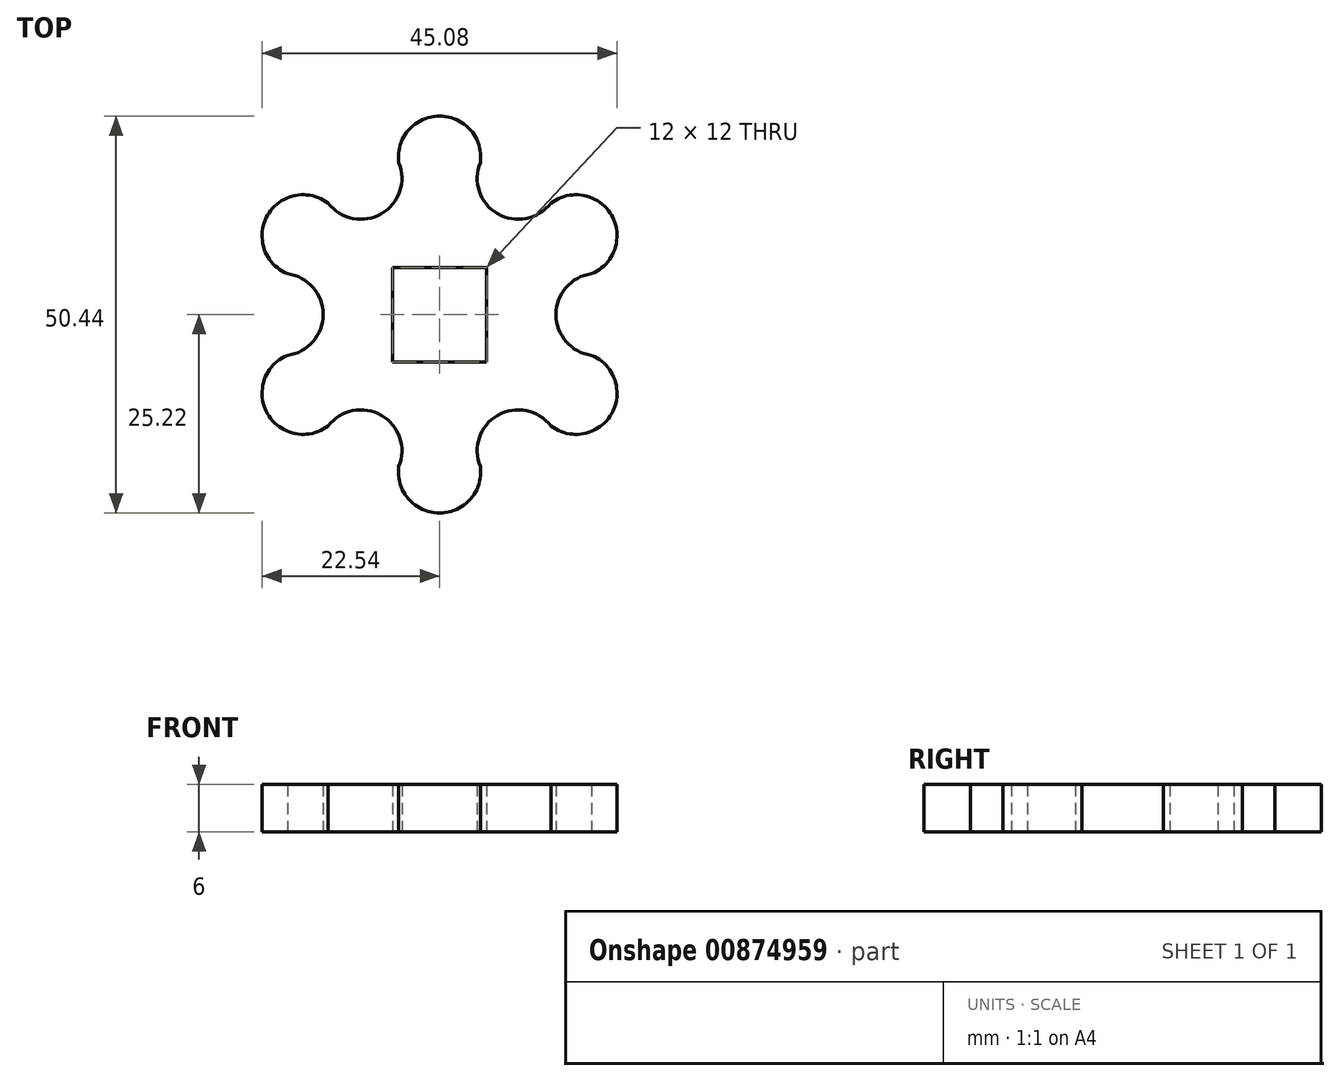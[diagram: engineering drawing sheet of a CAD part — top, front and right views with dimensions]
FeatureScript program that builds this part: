
annotation { "Feature Type Name" : "Feature", "Feature Type Description" : "" }
export const myFeature = defineFeature(function(context is Context, id is Id, definition is map)
    precondition{}
    {
        {
            var Q0;
            Q0=qCreatedBy(makeId("Top.planeOp"),FACE);
            var sketch = newSketch(context, id + "F0", { "sketchPlane" : qUnion([Q0])});
            skLineSegment(sketch, "E0.bottom", {"start": v(6, 6) * mm, "end": v(-6, 6) * mm});
            skLineSegment(sketch, "E0.top", {"start": v(6, -6) * mm, "end": v(-6, -6) * mm});
            skLineSegment(sketch, "E0.left", {"start": v(6, 6) * mm, "end": v(6, -6) * mm});
            skLineSegment(sketch, "E0.right", {"start": v(-6, 6) * mm, "end": v(-6, -6) * mm});
            skPoint(sketch, "E0.middle", {"position": v(0, 0) * mm});
            skCircle(sketch, "E1", {"center": v(0, 0) * mm, "radius": 20 * mm});
            skCircle(sketch, "E2", {"center": v(0, 20) * mm, "radius": 5.22 * mm});
            skCircle(sketch, "E3.1.0", {"center": v(-10, 17.32) * mm, "radius": 5.22 * mm});
            skCircle(sketch, "E3.2.0", {"center": v(-17.32, 10) * mm, "radius": 5.22 * mm});
            skCircle(sketch, "E3.3.0", {"center": v(-20, 0) * mm, "radius": 5.22 * mm});
            skCircle(sketch, "E3.4.0", {"center": v(-17.32, -10) * mm, "radius": 5.22 * mm});
            skCircle(sketch, "E3.5.0", {"center": v(-10, -17.32) * mm, "radius": 5.22 * mm});
            skCircle(sketch, "E3.6.0", {"center": v(0, -20) * mm, "radius": 5.22 * mm});
            skCircle(sketch, "E3.7.0", {"center": v(10, -17.32) * mm, "radius": 5.22 * mm});
            skCircle(sketch, "E3.8.0", {"center": v(17.32, -10) * mm, "radius": 5.22 * mm});
            skCircle(sketch, "E3.9.0", {"center": v(20, 0) * mm, "radius": 5.22 * mm});
            skCircle(sketch, "E3.10.0", {"center": v(17.32, 10) * mm, "radius": 5.22 * mm});
            skCircle(sketch, "E3.11.0", {"center": v(10, 17.32) * mm, "radius": 5.22 * mm});
            skPoint(sketch, "E4", {"position": v(5.18, 19.32) * mm});
            skSolve(sketch);
        }
        {
            var Q0;
            Q0=makeQuery(id+"F0.imprint","IMPRINT",FACE,{"disambiguationData":[TD([[makeQuery(id+"F0.imprint","IMPRINT",EDGE,{"derivedFrom":sQuery(id+"F0.wireOp",EDGE,"E0.bottom")}),-1.0]])]});
            var Q1;
            {var subQ0=sQuery(id+"F0.wireOp",EDGE,"E3.10.0");var subQ1=sQuery(id+"F0.wireOp",EDGE,"E3.9.0");var subQ6=makeQuery(id+"F0.imprint","INTERSECT",VERTEX,{"derivedFrom":[subQ1,subQ0]});Q1=makeQuery(id+"F0.imprint","IMPRINT",FACE,{"disambiguationData":[TD([[makeQuery(id+"F0.imprint","IMPRINT",EDGE,{"disambiguationData":[TD([[subQ6,1.0]])],"derivedFrom":subQ0}),1.0]])]});}
            var Q2;
            {var subQ1=sQuery(id+"F0.wireOp",EDGE,"E2");var subQ4=sQuery(id+"F0.wireOp",EDGE,"E3.1.0");var subQ6=makeQuery(id+"F0.imprint","INTERSECT",VERTEX,{"derivedFrom":[subQ1,subQ4]});Q2=makeQuery(id+"F0.imprint","IMPRINT",FACE,{"disambiguationData":[TD([[makeQuery(id+"F0.imprint","IMPRINT",EDGE,{"disambiguationData":[TD([[subQ6,-1.0]])],"derivedFrom":subQ1}),1.0]])]});}
            var Q3;
            {var subQ1=sQuery(id+"F0.wireOp",EDGE,"E3.8.0");var subQ4=sQuery(id+"F0.wireOp",EDGE,"E3.7.0");var subQ6=makeQuery(id+"F0.imprint","INTERSECT",VERTEX,{"derivedFrom":[subQ4,subQ1]});Q3=makeQuery(id+"F0.imprint","IMPRINT",FACE,{"disambiguationData":[TD([[makeQuery(id+"F0.imprint","IMPRINT",EDGE,{"disambiguationData":[TD([[subQ6,1.0]])],"derivedFrom":subQ1}),1.0]])]});}
            var Q4;
            {var subQ0=sQuery(id+"F0.wireOp",EDGE,"E3.4.0");var subQ1=sQuery(id+"F0.wireOp",EDGE,"E3.3.0");var subQ6=makeQuery(id+"F0.imprint","INTERSECT",VERTEX,{"derivedFrom":[subQ1,subQ0]});Q4=makeQuery(id+"F0.imprint","IMPRINT",FACE,{"disambiguationData":[TD([[makeQuery(id+"F0.imprint","IMPRINT",EDGE,{"disambiguationData":[TD([[subQ6,1.0]])],"derivedFrom":subQ0}),1.0]])]});}
            var Q5;
            {var subQ0=sQuery(id+"F0.wireOp",EDGE,"E3.2.0");var subQ1=sQuery(id+"F0.wireOp",EDGE,"E3.1.0");var subQ6=makeQuery(id+"F0.imprint","INTERSECT",VERTEX,{"derivedFrom":[subQ1,subQ0]});Q5=makeQuery(id+"F0.imprint","IMPRINT",FACE,{"disambiguationData":[TD([[makeQuery(id+"F0.imprint","IMPRINT",EDGE,{"disambiguationData":[TD([[subQ6,1.0]])],"derivedFrom":subQ0}),1.0]])]});}
            var Q6;
            {var subQ0=sQuery(id+"F0.wireOp",EDGE,"E2");var subQ1=sQuery(id+"F0.wireOp",EDGE,"E1");var subQ2=makeQuery(id+"F0.imprint","INTERSECT",VERTEX,{"derivedFrom":[subQ1,subQ0,sQuery(id+"F0.wireOp",EDGE,"E3.11.0")]});Q6=makeQuery(id+"F0.imprint","IMPRINT",FACE,{"disambiguationData":[TD([[makeQuery(id+"F0.imprint","IMPRINT",EDGE,{"disambiguationData":[TD([[subQ2,-1.0]])],"derivedFrom":subQ1}),-1.0]])]});}
            var Q7;
            {var subQ0=sQuery(id+"F0.wireOp",EDGE,"E3.10.0");var subQ1=sQuery(id+"F0.wireOp",EDGE,"E1");var subQ2=makeQuery(id+"F0.imprint","INTERSECT",VERTEX,{"derivedFrom":[subQ1,sQuery(id+"F0.wireOp",EDGE,"E3.9.0"),subQ0]});Q7=makeQuery(id+"F0.imprint","IMPRINT",FACE,{"disambiguationData":[TD([[makeQuery(id+"F0.imprint","IMPRINT",EDGE,{"disambiguationData":[TD([[subQ2,-1.0]])],"derivedFrom":subQ1}),-1.0]])]});}
            var Q8;
            {var subQ0=sQuery(id+"F0.wireOp",EDGE,"E3.8.0");var subQ1=sQuery(id+"F0.wireOp",EDGE,"E1");var subQ2=makeQuery(id+"F0.imprint","INTERSECT",VERTEX,{"derivedFrom":[subQ1,subQ0,sQuery(id+"F0.wireOp",EDGE,"E3.9.0")]});Q8=makeQuery(id+"F0.imprint","IMPRINT",FACE,{"disambiguationData":[TD([[makeQuery(id+"F0.imprint","IMPRINT",EDGE,{"disambiguationData":[TD([[subQ2,1.0]])],"derivedFrom":subQ1}),-1.0]])]});}
            var Q9;
            {var subQ0=sQuery(id+"F0.wireOp",EDGE,"E3.6.0");var subQ1=sQuery(id+"F0.wireOp",EDGE,"E3.5.0");var subQ6=makeQuery(id+"F0.imprint","INTERSECT",VERTEX,{"derivedFrom":[subQ1,subQ0]});Q9=makeQuery(id+"F0.imprint","IMPRINT",FACE,{"disambiguationData":[TD([[makeQuery(id+"F0.imprint","IMPRINT",EDGE,{"disambiguationData":[TD([[subQ6,1.0]])],"derivedFrom":subQ0}),1.0]])]});}
            var Q10;
            {var subQ0=sQuery(id+"F0.wireOp",EDGE,"E3.6.0");var subQ1=sQuery(id+"F0.wireOp",EDGE,"E1");var subQ2=makeQuery(id+"F0.imprint","INTERSECT",VERTEX,{"derivedFrom":[subQ1,sQuery(id+"F0.wireOp",EDGE,"E3.5.0"),subQ0]});Q10=makeQuery(id+"F0.imprint","IMPRINT",FACE,{"disambiguationData":[TD([[makeQuery(id+"F0.imprint","IMPRINT",EDGE,{"disambiguationData":[TD([[subQ2,-1.0]])],"derivedFrom":subQ1}),-1.0]])]});}
            var Q11;
            {var subQ0=sQuery(id+"F0.wireOp",EDGE,"E3.4.0");var subQ1=sQuery(id+"F0.wireOp",EDGE,"E1");var subQ2=makeQuery(id+"F0.imprint","INTERSECT",VERTEX,{"derivedFrom":[subQ1,sQuery(id+"F0.wireOp",EDGE,"E3.3.0"),subQ0]});Q11=makeQuery(id+"F0.imprint","IMPRINT",FACE,{"disambiguationData":[TD([[makeQuery(id+"F0.imprint","IMPRINT",EDGE,{"disambiguationData":[TD([[subQ2,-1.0]])],"derivedFrom":subQ1}),-1.0]])]});}
            var Q12;
            {var subQ0=sQuery(id+"F0.wireOp",EDGE,"E3.2.0");var subQ1=sQuery(id+"F0.wireOp",EDGE,"E1");var subQ2=makeQuery(id+"F0.imprint","INTERSECT",VERTEX,{"derivedFrom":[subQ1,sQuery(id+"F0.wireOp",EDGE,"E3.1.0"),subQ0]});Q12=makeQuery(id+"F0.imprint","IMPRINT",FACE,{"disambiguationData":[TD([[makeQuery(id+"F0.imprint","IMPRINT",EDGE,{"disambiguationData":[TD([[subQ2,-1.0]])],"derivedFrom":subQ1}),-1.0]])]});}
            extrude(context, id + "F1", {"entities" : qUnion([Q0, Q1, Q2, Q3, Q4, Q5, Q6, Q7, Q8, Q9, Q10, Q11, Q12]), "depth" : 6 * mm, "offsetDistance" : 25 * mm});
        }
    });
